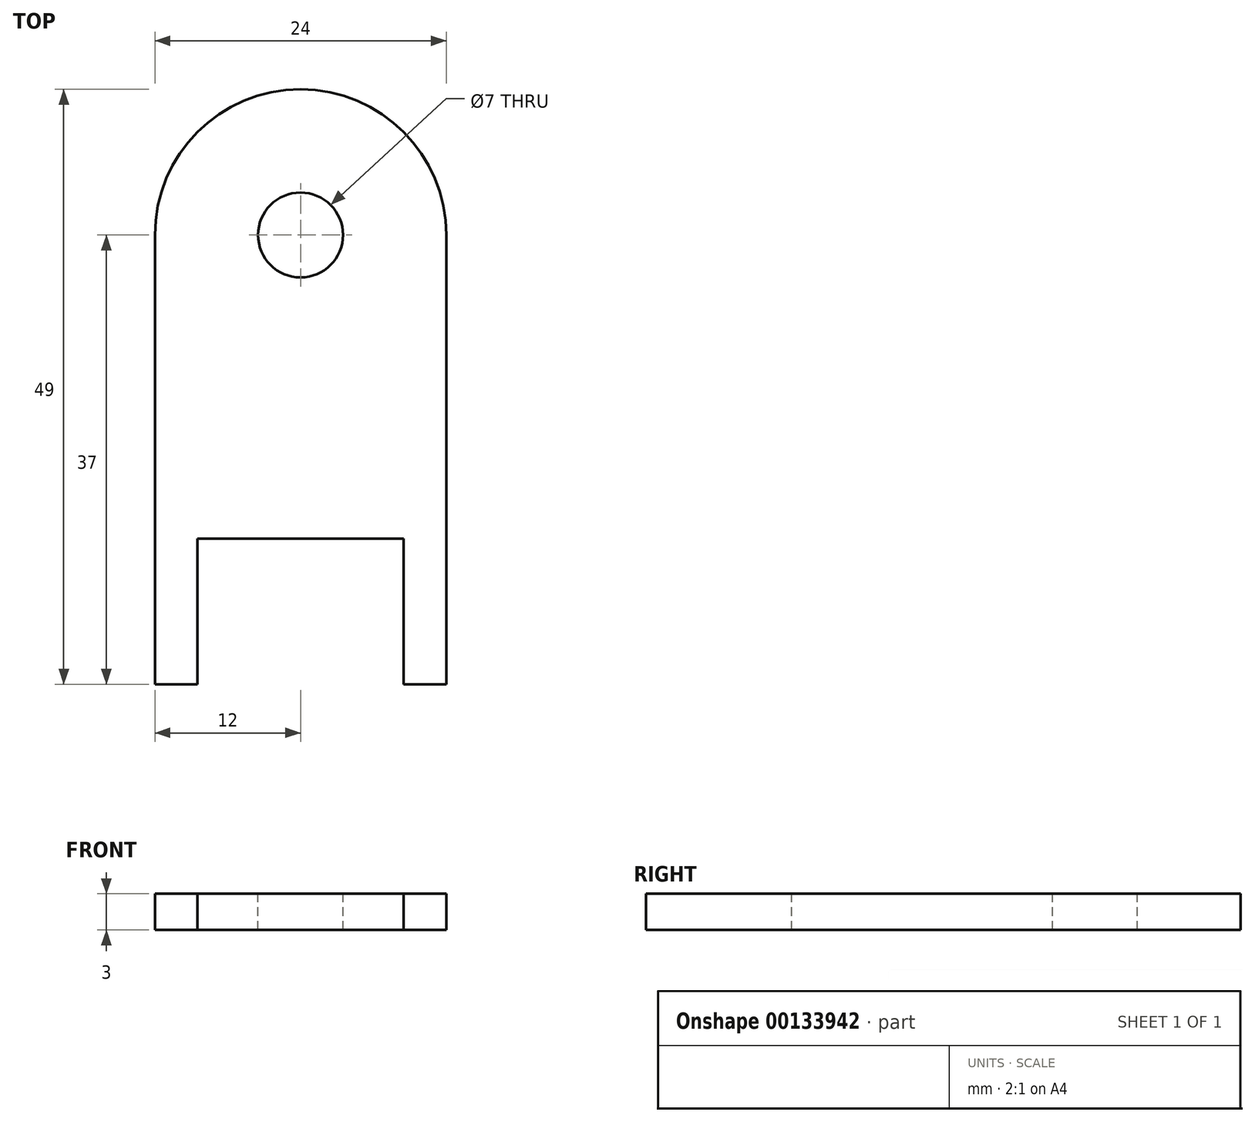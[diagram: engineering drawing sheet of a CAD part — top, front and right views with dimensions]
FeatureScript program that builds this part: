
annotation { "Feature Type Name" : "Feature", "Feature Type Description" : "" }
export const myFeature = defineFeature(function(context is Context, id is Id, definition is map)
    precondition{}
    {
        {
            var Q0;
            Q0=qCreatedBy(makeId("Top.planeOp"),FACE);
            var sketch = newSketch(context, id + "F0", { "sketchPlane" : qUnion([Q0])});
            skArc(sketch, "E0", {"start": v(12, 0) * mm, "mid": v(0, 12) * mm, "end": v(-12, 0) * mm});
            skCircle(sketch, "E1", {"center": v(0, 0) * mm, "radius": 3.5 * mm});
            skCircle(sketch, "E2", {"center": v(0, 0) * mm, "radius": 6.15 * mm});
            skLineSegment(sketch, "E3", {"start": v(-12, 0) * mm, "end": v(-12, -37) * mm});
            skLineSegment(sketch, "E4", {"start": v(-12, -37) * mm, "end": v(-12, -37) * mm});
            skLineSegment(sketch, "E5", {"start": v(12, 0) * mm, "end": v(12, -37) * mm});
            skLineSegment(sketch, "E6", {"start": v(-12, -25) * mm, "end": v(12, -25) * mm});
            skLineSegment(sketch, "E7", {"start": v(8.5, -37) * mm, "end": v(8.5, 8.47) * mm});
            skLineSegment(sketch, "E8", {"start": v(-8.5, -37) * mm, "end": v(-8.5, -37) * mm});
            skLineSegment(sketch, "E9", {"start": v(-8.5, -37) * mm, "end": v(-8.5, 8.47) * mm});
            skLineSegment(sketch, "E10", {"start": v(-12, -37) * mm, "end": v(-8.5, -37) * mm});
            skLineSegment(sketch, "E11", {"start": v(-8.5, -37) * mm, "end": v(8.5, -37) * mm, "construction": true});
            skLineSegment(sketch, "E12", {"start": v(8.5, -37) * mm, "end": v(12, -37) * mm});
            skLineSegment(sketch, "E13", {"start": v(-12.17, 12) * mm, "end": v(11, 12) * mm, "construction": true});
            skPoint(sketch, "E13.startSnap0", {"position": v(0, 12) * mm});
            skSolve(sketch);
        }
        {
            var Q0;
            {var subQ0=sQuery(id+"F0.wireOp",EDGE,"E12");Q0=makeQuery(id+"F0.imprint","IMPRINT",FACE,{"disambiguationData":[TD([[makeQuery(id+"F0.imprint","IMPRINT",EDGE,{"derivedFrom":subQ0}),1.0]])]});}
            var Q1;
            {var subQ0=sQuery(id+"F0.wireOp",EDGE,"E5");var subQ1=sQuery(id+"F0.wireOp",EDGE,"E0");var subQ2=makeQuery(id+"F0.imprint","INTERSECT",VERTEX,{"derivedFrom":[subQ1,subQ0]});Q1=makeQuery(id+"F0.imprint","IMPRINT",FACE,{"disambiguationData":[TD([[makeQuery(id+"F0.imprint","IMPRINT",EDGE,{"disambiguationData":[TD([[subQ2,-1.0]])],"derivedFrom":subQ1}),1.0]])]});}
            var Q2;
            Q2=makeQuery(id+"F0.imprint","IMPRINT",FACE,{"disambiguationData":[TD([[makeQuery(id+"F0.imprint","IMPRINT",EDGE,{"derivedFrom":sQuery(id+"F0.wireOp",EDGE,"E1")}),-1.0]])]});
            var Q3;
            Q3=makeQuery(id+"F0.imprint","IMPRINT",FACE,{"disambiguationData":[TD([[makeQuery(id+"F0.imprint","IMPRINT",EDGE,{"derivedFrom":sQuery(id+"F0.wireOp",EDGE,"E2")}),-1.0]])]});
            var Q4;
            {var subQ0=sQuery(id+"F0.wireOp",EDGE,"E3");var subQ1=sQuery(id+"F0.wireOp",EDGE,"E0");var subQ2=makeQuery(id+"F0.imprint","INTERSECT",VERTEX,{"derivedFrom":[subQ1,subQ0]});Q4=makeQuery(id+"F0.imprint","IMPRINT",FACE,{"disambiguationData":[TD([[makeQuery(id+"F0.imprint","IMPRINT",EDGE,{"disambiguationData":[TD([[subQ2,1.0]])],"derivedFrom":subQ1}),1.0]])]});}
            var Q5;
            {var subQ0=sQuery(id+"F0.wireOp",EDGE,"E10");Q5=makeQuery(id+"F0.imprint","IMPRINT",FACE,{"disambiguationData":[TD([[makeQuery(id+"F0.imprint","IMPRINT",EDGE,{"derivedFrom":subQ0}),1.0]])]});}
            extrude(context, id + "F1", {"entities" : qUnion([Q0, Q1, Q2, Q3, Q4, Q5]), "oppositeDirection" : true, "depth" : 3 * mm});
        }
    });
